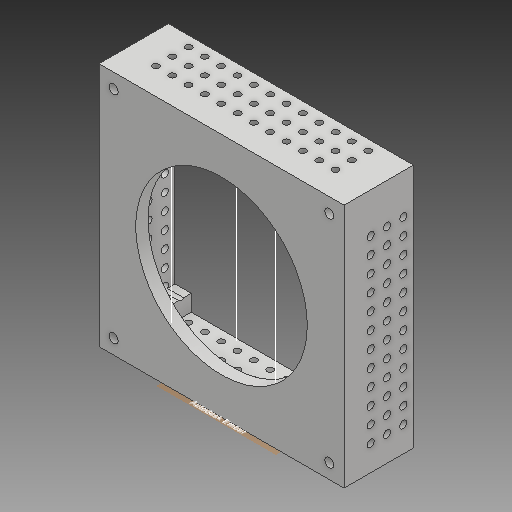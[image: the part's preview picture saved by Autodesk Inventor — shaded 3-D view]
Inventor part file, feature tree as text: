
AUTODESK INVENTOR PART (.ipt)
format: ipt  version: 2018 (Build 220112000, 112)  size: 508,928 bytes
history: native  units: mm
features: sketch x8, extrude x5, pattern_linear x2
ambient origin geometry x8: Origin, YZ Plane, XZ Plane, XY Plane, X Axis, Y Axis, Z Axis, Center Point
bodies: Solid1 (feature_tree)
feature tree (15):
  sketch  "Sketch1"  dims[d0=150.0mm d1=150.0mm]
  extrude  "Extrusion1"  Depth=150.0mm
  extrude  "Extrusion3"  Depth=4.0mm
  extrude  "Extrusion4"  Depth=10.0mm
  pattern_linear  "Rectangular Pattern1"  Count1=2 Spacing1=132.0mm
  extrude  "Extrusion5"  Depth=132.0mm
  pattern_linear  "Rectangular Pattern2"  Count1=8 Spacing1=0.0mm
  sketch  "Sketch9"  dims[d17=20.0mm d19=132.0mm d20=5.5mm d21=80.0mm d22=0.0mm]
  extrude  "Extrusion8"  Depth=132.0mm
  sketch  "Sketch11"  dims[d45=4.0mm d46=40.0mm d47=0.0mm]
  sketch  "Sketch2"  dims[d2=7.5mm d3=0.0mm d7=4.0mm]
  sketch  "Sketch4"  dims[d8=35.0mm d9=0.0mm d10=10.0mm]
  sketch  "Sketch5"  dims[d11=10.0mm]
  sketch  "Sketch6"  dims[d12=35.0mm d13=0.0mm d14=20.0mm d16=132.0mm]
  sketch  "Sketch10"  dims[d23=20.0mm d25=132.0mm d26=20.0mm d28=132.0mm]
